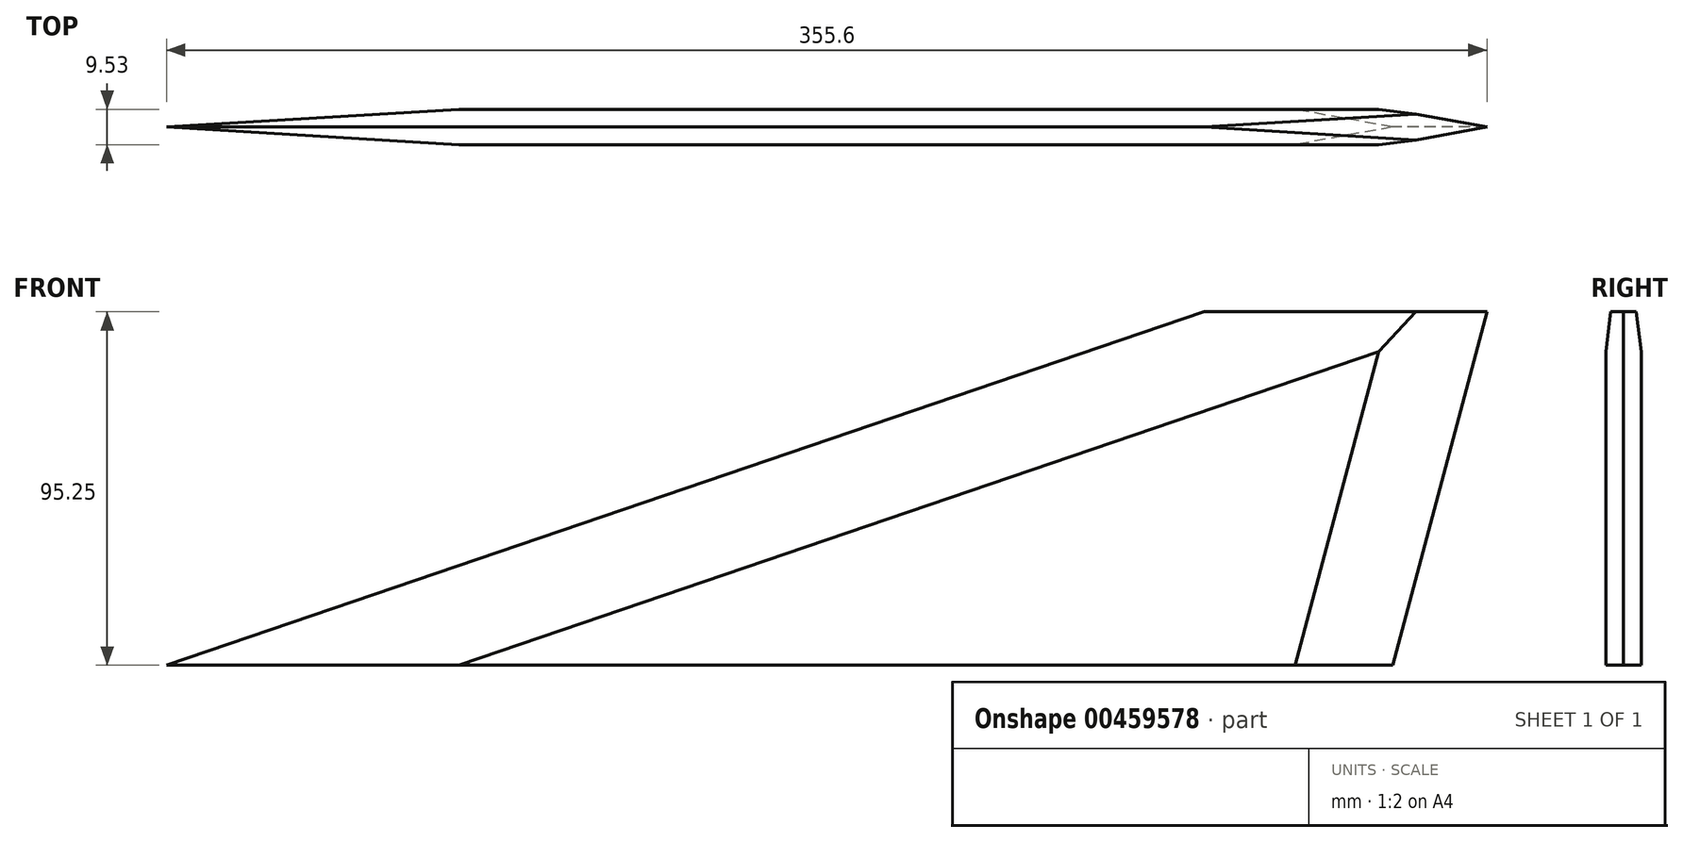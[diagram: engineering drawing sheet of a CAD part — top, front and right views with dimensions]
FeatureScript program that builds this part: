
annotation { "Feature Type Name" : "Feature", "Feature Type Description" : "" }
export const myFeature = defineFeature(function(context is Context, id is Id, definition is map)
    precondition{}
    {
        {
            var Q0;
            Q0=qCreatedBy(makeId("Front.planeOp"),FACE);
            var sketch = newSketch(context, id + "F0", { "sketchPlane" : qUnion([Q0])});
            skLineSegment(sketch, "E0", {"start": v(-167, -29.9) * mm, "end": v(163.2, -29.9) * mm});
            skLineSegment(sketch, "E1", {"start": v(163.2, -29.9) * mm, "end": v(188.6, 65.36) * mm});
            skLineSegment(sketch, "E2", {"start": v(188.6, 65.36) * mm, "end": v(112.4, 65.36) * mm});
            skLineSegment(sketch, "E3", {"start": v(112.4, 65.36) * mm, "end": v(-167, -29.9) * mm});
            skSolve(sketch);
        }
        {
            var Q0;
            Q0 = qSketchRegion(id + "F0", true);
            extrude(context, id + "F1", {"entities" : qUnion([Q0]), "depth" : 9.52 * mm});
        }
        {
            var Q0;
            Q0=makeQuery(id+"F1.opExtrude","CAP_EDGE",EDGE,{"disambiguationData":[OSD([sQuery(id+"F0.wireOp",EDGE,"E3")])],"isStart":false});
            chamfer(context, id + "F2", {"entities" : qUnion([Q0]), "chamferType" : ChamferType.TWO_OFFSETS, "width1" : 25.4 * mm, "oppositeDirection" : false, "width2" : 4.76 * mm, "tangentPropagation" : true});
        }
        {
            var Q0;
            Q0=makeQuery(id+"F1.opExtrude","CAP_EDGE",EDGE,{"disambiguationData":[OSD([sQuery(id+"F0.wireOp",EDGE,"E3")])],"isStart":true});
            chamfer(context, id + "F3", {"entities" : qUnion([Q0]), "chamferType" : ChamferType.TWO_OFFSETS, "width1" : 4.76 * mm, "oppositeDirection" : false, "width2" : 25.4 * mm, "tangentPropagation" : true});
        }
        {
            var Q0;
            Q0=makeQuery(id+"F1.opExtrude","CAP_EDGE",EDGE,{"disambiguationData":[OSD([sQuery(id+"F0.wireOp",EDGE,"E1")])],"isStart":false});
            chamfer(context, id + "F4", {"entities" : qUnion([Q0]), "chamferType" : ChamferType.TWO_OFFSETS, "width1" : 25.4 * mm, "oppositeDirection" : false, "width2" : 4.76 * mm, "tangentPropagation" : true});
        }
        {
            var Q0;
            Q0=makeQuery(id+"F1.opExtrude","CAP_EDGE",EDGE,{"disambiguationData":[OSD([sQuery(id+"F0.wireOp",EDGE,"E1")])],"isStart":true});
            chamfer(context, id + "F5", {"entities" : qUnion([Q0]), "chamferType" : ChamferType.TWO_OFFSETS, "width1" : 4.76 * mm, "oppositeDirection" : false, "width2" : 25.4 * mm, "tangentPropagation" : true});
        }
    });
